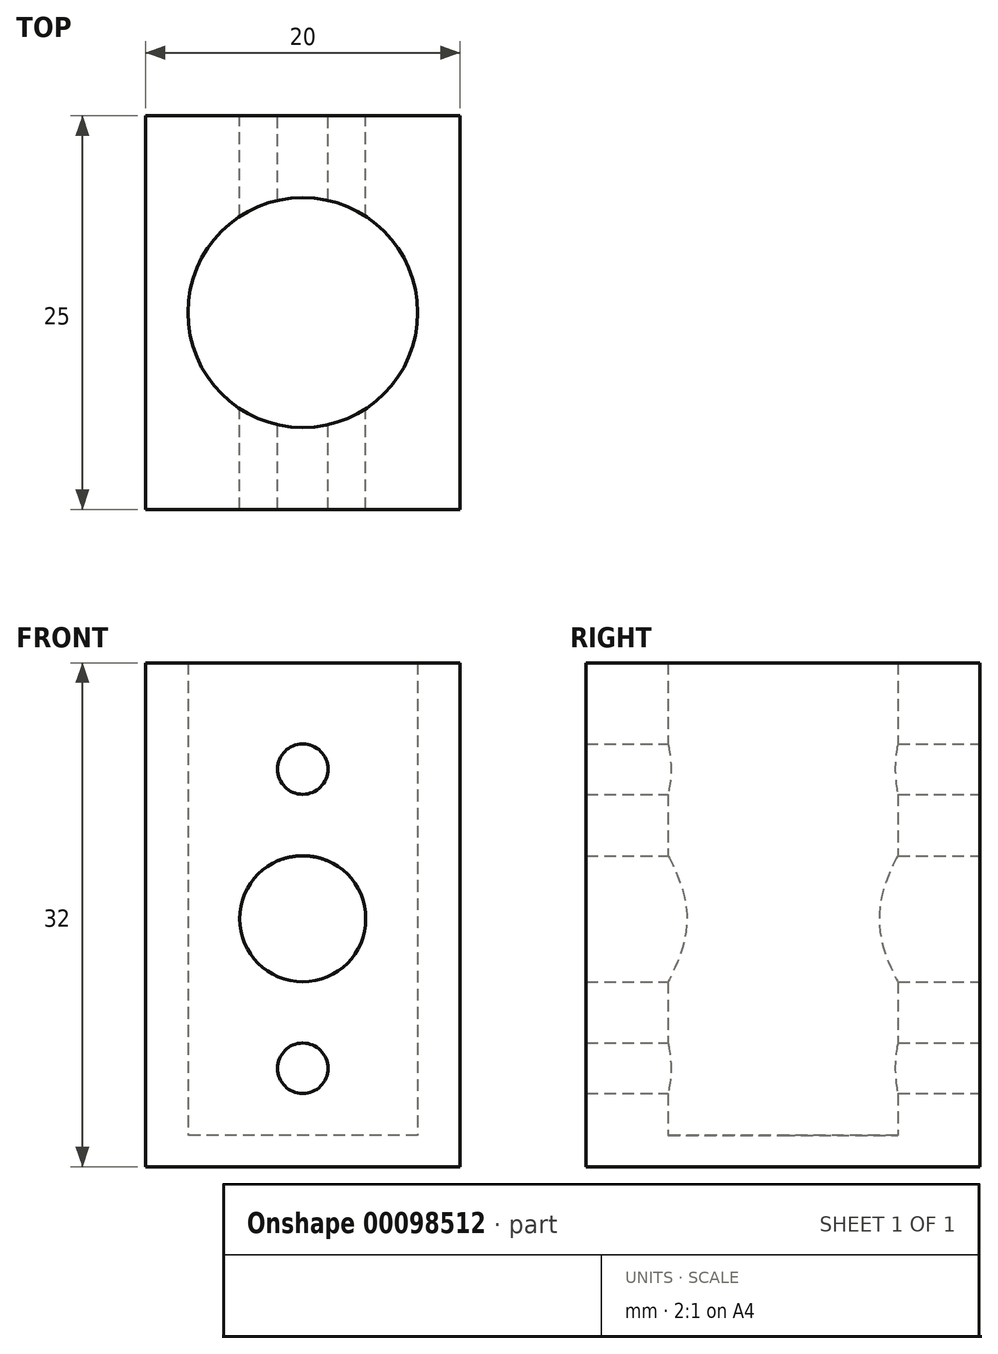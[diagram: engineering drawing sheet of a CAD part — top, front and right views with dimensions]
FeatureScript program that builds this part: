
annotation { "Feature Type Name" : "Feature", "Feature Type Description" : "" }
export const myFeature = defineFeature(function(context is Context, id is Id, definition is map)
    precondition{}
    {
        {
            var Q0;
            Q0=qCreatedBy(makeId("Top.planeOp"),FACE);
            var sketch = newSketch(context, id + "F0", { "sketchPlane" : qUnion([Q0])});
            skLineSegment(sketch, "E0.bottom", {"start": v(10, 12.5) * mm, "end": v(-10, 12.5) * mm});
            skLineSegment(sketch, "E0.top", {"start": v(10, -12.5) * mm, "end": v(-10, -12.5) * mm});
            skLineSegment(sketch, "E0.left", {"start": v(10, 12.5) * mm, "end": v(10, -12.5) * mm});
            skLineSegment(sketch, "E0.right", {"start": v(-10, 12.5) * mm, "end": v(-10, -12.5) * mm});
            skPoint(sketch, "E0.middle", {"position": v(0, 0) * mm});
            skCircle(sketch, "E1", {"center": v(0, 0) * mm, "radius": 7.3 * mm});
            skSolve(sketch);
        }
        {
            var Q0;
            Q0=makeQuery(id+"F0.imprint","IMPRINT",FACE,{"disambiguationData":[TD([[makeQuery(id+"F0.imprint","IMPRINT",EDGE,{"derivedFrom":sQuery(id+"F0.wireOp",EDGE,"E0.bottom")}),1.0]])]});
            extrude(context, id + "F1", {"entities" : qUnion([Q0]), "depth" : 30 * mm});
        }
        {
            var Q0;
            Q0=makeQuery(id+"F1.opExtrude","SWEPT_FACE",FACE,{"disambiguationData":[OSD([sQuery(id+"F0.wireOp",EDGE,"E0.left")])]});
            var sketch = newSketch(context, id + "F2", { "sketchPlane" : qUnion([Q0])});
            skLineSegment(sketch, "E2", {"start": v(0, 0) * mm, "end": v(0, 6) * mm});
            skPoint(sketch, "E2.endSnap0", {"position": v(0, 0) * mm});
            skCircle(sketch, "E3", {"center": v(0, 6) * mm, "radius": 1.1 * mm});
            skLineSegment(sketch, "E4", {"start": v(0, 6) * mm, "end": v(0, 12) * mm});
            skCircle(sketch, "E5", {"center": v(0, 12) * mm, "radius": 1.1 * mm});
            skSolve(sketch);
        }
        {
            var Q0;
            Q0=makeQuery(id+"F1.opExtrude","SWEPT_FACE",FACE,{"disambiguationData":[OSD([sQuery(id+"F0.wireOp",EDGE,"E0.bottom")])]});
            var sketch = newSketch(context, id + "F3", { "sketchPlane" : qUnion([Q0])});
            skLineSegment(sketch, "E6", {"start": v(0, 0) * mm, "end": v(0, 4.25) * mm});
            skPoint(sketch, "E6.endSnap0", {"position": v(0, 0) * mm});
            skCircle(sketch, "E7", {"center": v(0, 4.25) * mm, "radius": 1.6 * mm});
            skLineSegment(sketch, "E8", {"start": v(0, 4.25) * mm, "end": v(0, 23.25) * mm});
            skCircle(sketch, "E9", {"center": v(0, 23.25) * mm, "radius": 1.6 * mm});
            skCircle(sketch, "E10", {"center": v(0, 13.75) * mm, "radius": 4 * mm});
            skSolve(sketch);
        }
        {
            var Q0;
            Q0=qSketchRegion(id+"F3",true);
            extrude(context, id + "F4", {"entities" : qUnion([Q0]), "operationType" : NewBodyOperationType.REMOVE, "endBound" : BoundingType.THROUGH_ALL, "oppositeDirection" : true, "depth" : 25 * mm});
        }
        {
            var Q0;
            Q0=makeQuery(id+"F1.opExtrude","CAP_FACE",FACE,{"disambiguationData":[OSD([sQuery(id+"F0.wireOp",EDGE,"E0.bottom"),sQuery(id+"F0.wireOp",EDGE,"E0.top"),sQuery(id+"F0.wireOp",EDGE,"E0.left"),sQuery(id+"F0.wireOp",EDGE,"E0.right"),sQuery(id+"F0.wireOp",EDGE,"E1")])],"isStart":true});
            var sketch = newSketch(context, id + "F5", { "sketchPlane" : qUnion([Q0])});
            skLineSegment(sketch, "E11.bottom", {"start": v(-10, -12.5) * mm, "end": v(10, -12.5) * mm});
            skLineSegment(sketch, "E11.top", {"start": v(-10, 12.5) * mm, "end": v(10, 12.5) * mm});
            skLineSegment(sketch, "E11.left", {"start": v(-10, -12.5) * mm, "end": v(-10, 12.5) * mm});
            skLineSegment(sketch, "E11.right", {"start": v(10, -12.5) * mm, "end": v(10, 12.5) * mm});
            skSolve(sketch);
        }
        {
            var Q0;
            Q0=qSketchRegion(id+"F5",true);
            extrude(context, id + "F6", {"entities" : qUnion([Q0]), "operationType" : NewBodyOperationType.ADD, "depth" : 2 * mm});
        }
    });
